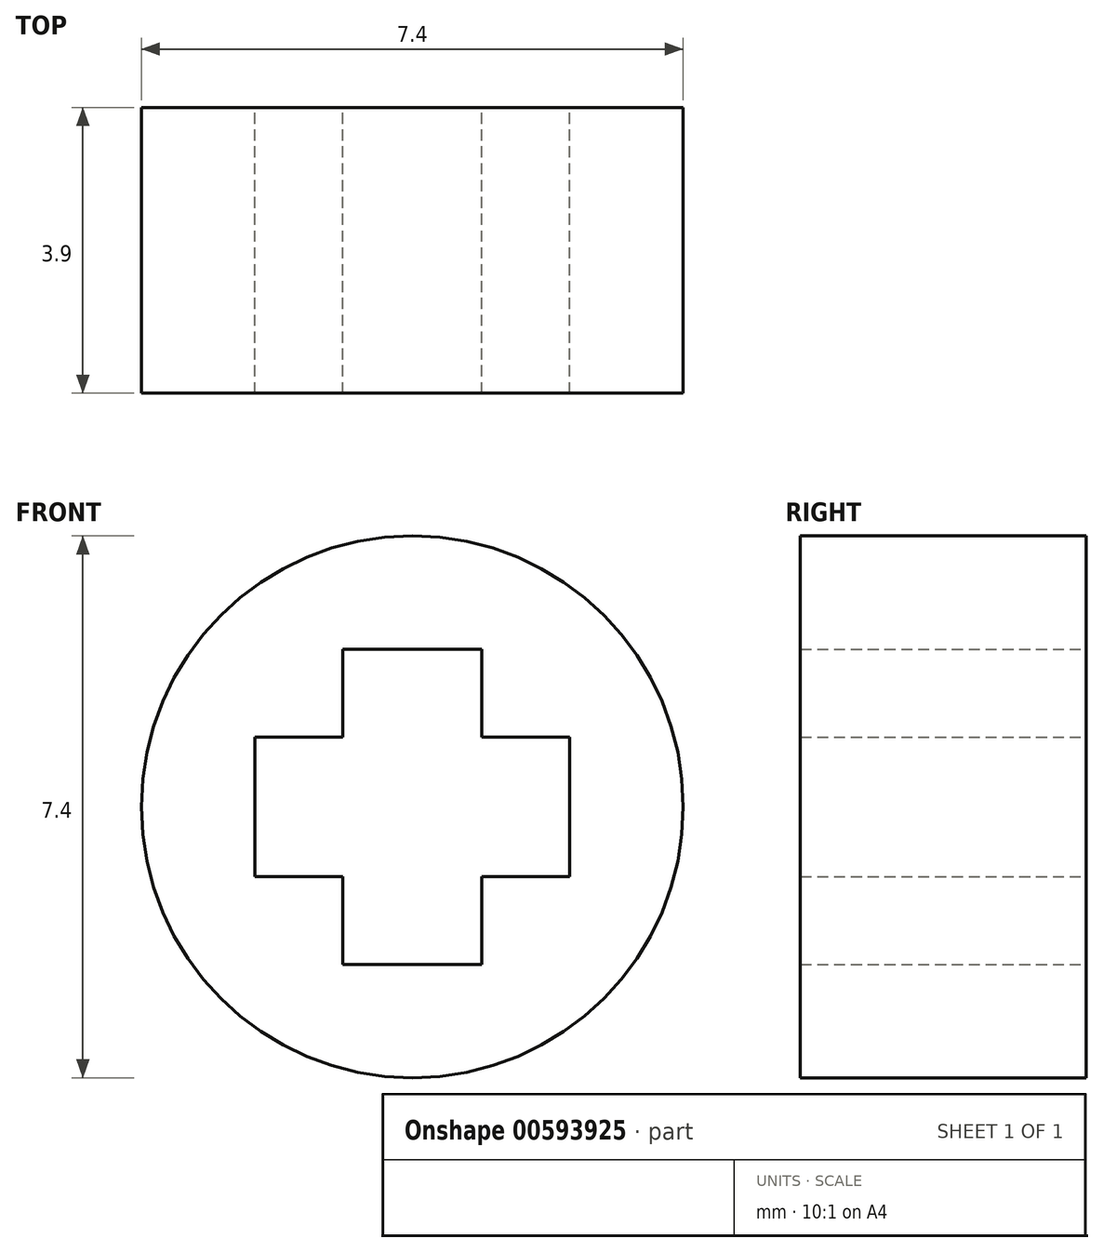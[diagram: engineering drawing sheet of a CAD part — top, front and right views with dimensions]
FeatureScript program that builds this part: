
annotation { "Feature Type Name" : "Feature", "Feature Type Description" : "" }
export const myFeature = defineFeature(function(context is Context, id is Id, definition is map)
    precondition{}
    {
        {
            var Q0;
            Q0=qCreatedBy(makeId("Front.planeOp"),FACE);
            var sketch = newSketch(context, id + "F0", { "sketchPlane" : qUnion([Q0])});
            skLineSegment(sketch, "E0", {"start": v(0, 3.05) * mm, "end": v(-0.95, 3.05) * mm});
            skLineSegment(sketch, "E1", {"start": v(0, 3.05) * mm, "end": v(0.95, 3.05) * mm});
            skLineSegment(sketch, "E2", {"start": v(-0.95, 3.05) * mm, "end": v(-0.95, 1.85) * mm});
            skLineSegment(sketch, "E3", {"start": v(-0.95, 1.85) * mm, "end": v(-2.15, 1.85) * mm});
            skLineSegment(sketch, "E4", {"start": v(-2.15, 1.85) * mm, "end": v(-2.15, -0.05) * mm});
            skLineSegment(sketch, "E5", {"start": v(-2.15, -0.05) * mm, "end": v(-0.95, -0.05) * mm});
            skLineSegment(sketch, "E6", {"start": v(-0.95, -0.05) * mm, "end": v(-0.95, -1.25) * mm});
            skLineSegment(sketch, "E7", {"start": v(-0.95, -1.25) * mm, "end": v(0.95, -1.25) * mm});
            skLineSegment(sketch, "E8", {"start": v(0.95, -1.25) * mm, "end": v(0.95, -0.05) * mm});
            skLineSegment(sketch, "E9", {"start": v(0.95, -0.05) * mm, "end": v(2.15, -0.05) * mm});
            skLineSegment(sketch, "E10", {"start": v(2.15, -0.05) * mm, "end": v(2.15, 1.85) * mm});
            skLineSegment(sketch, "E11", {"start": v(2.15, 1.85) * mm, "end": v(0.95, 1.85) * mm});
            skLineSegment(sketch, "E12", {"start": v(0.95, 1.85) * mm, "end": v(0.95, 3.05) * mm});
            skLineSegment(sketch, "E13", {"start": v(-0.95, 1.85) * mm, "end": v(0.95, -0.05) * mm});
            skCircle(sketch, "E14", {"center": v(0, 0.9) * mm, "radius": 3.7 * mm});
            skSolve(sketch);
        }
        {
            var Q0;
            Q0=makeQuery(id+"F0.imprint","IMPRINT",FACE,{"disambiguationData":[TD([[makeQuery(id+"F0.imprint","IMPRINT",EDGE,{"derivedFrom":sQuery(id+"F0.wireOp",EDGE,"E0")}),-1.0]])]});
            extrude(context, id + "F1", {"entities" : qUnion([Q0]), "depth" : 3.9 * mm, "offsetDistance" : 25 * mm});
        }
    });
